# Revit family: РИДАН_Электронный комнатный термостат RSmart-SW
name_source: partatom
category: Оборудование
units: mm (PartAtom-declared; Revit-internal decimal feet)

## family parameters
Всегда вертикально = Да
Классификация = Нет
На основе рабочей плоскости = Да
Общий = Нет
При загрузке вырезать с полостями = Нет
Размер круглого соединителя = Использовать диаметр
Тип детали = Нормальный
Точка расчета площади = Нет

## types (1)
- РИДАН_Электронный комнатный термостат RSmart-SW
    ADSK_Версия Revit = 2019
    ADSK_Версия семейства = 1.0
    ADSK_Диаметр условный = 0 мм
    ADSK_Единица измерения = шт.
    ADSK_Завод-изготовитель = ООО «Ридан-Трейд»
    ADSK_Классификация нагрузок = Прочее
    ADSK_Код изделия = 088L1141R
    ADSK_Количество = 1
    ADSK_Коэффициент мощности = 1
    ADSK_Марка = RSmart-SW
    ADSK_Масса = 0
    ADSK_Наименование = Комнатный сенсорный термостат RSmart-SW с Wi-Fi подключением 230V, встраиваемый, белый
    ADSK_Напряжение = 24 В
    ADSK_Полная мощность = 1 В·А
    Отметка по умолчанию = 1219 мм
